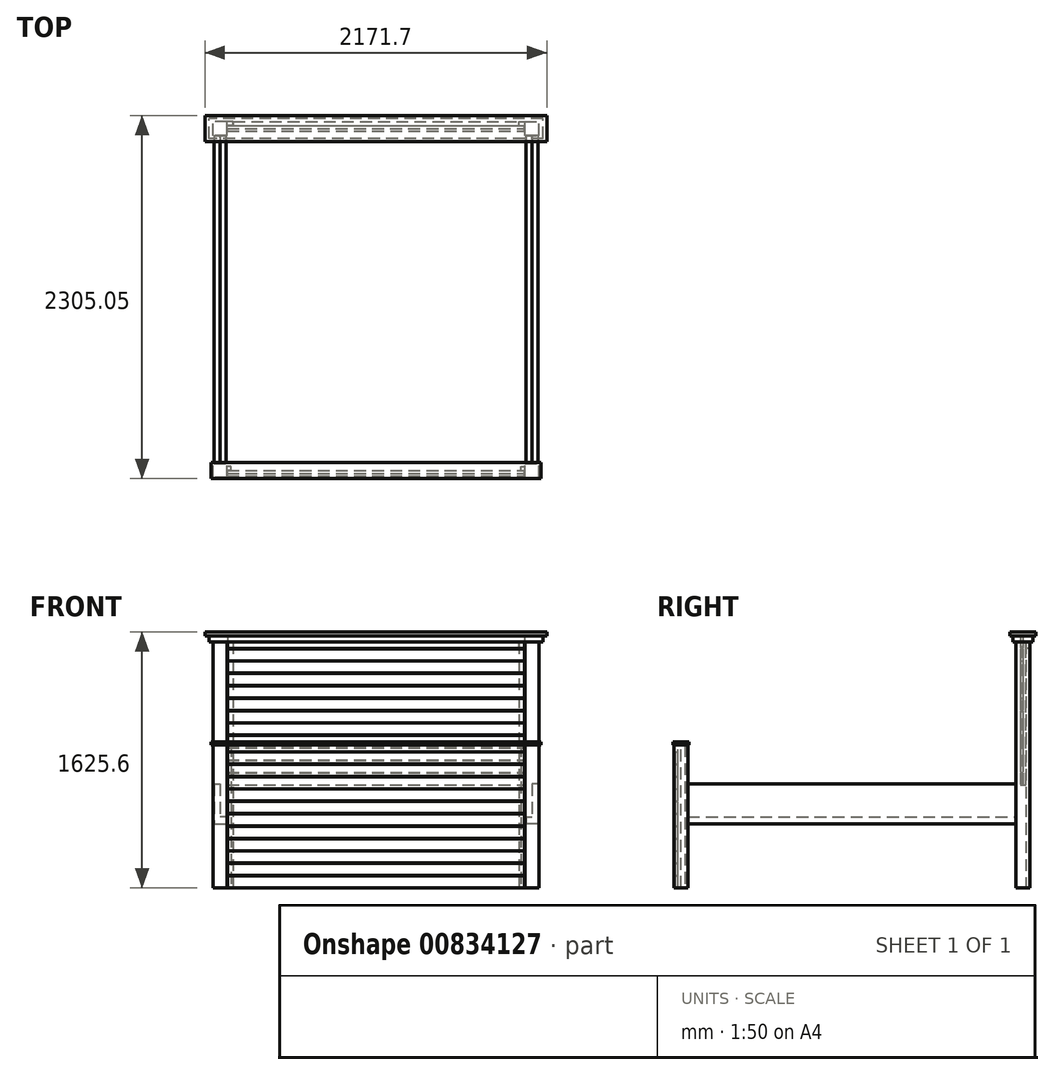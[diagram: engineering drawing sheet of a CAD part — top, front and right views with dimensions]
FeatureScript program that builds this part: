
annotation { "Feature Type Name" : "Feature", "Feature Type Description" : "" }
export const myFeature = defineFeature(function(context is Context, id is Id, definition is map)
    precondition{}
    {
        {
            var Q0;
            Q0=qCreatedBy(makeId("Top.planeOp"),FACE);
            var sketch = newSketch(context, id + "F0", { "sketchPlane" : qUnion([Q0])});
            skLineSegment(sketch, "E0.rect.bottom", {"start": v(44.45, -44.45) * mm, "end": v(-44.45, -44.45) * mm});
            skLineSegment(sketch, "E0.rect.top", {"start": v(44.45, 44.45) * mm, "end": v(-44.45, 44.45) * mm});
            skLineSegment(sketch, "E0.rect.left", {"start": v(44.45, -44.45) * mm, "end": v(44.45, 44.45) * mm});
            skLineSegment(sketch, "E0.rect.right", {"start": v(-44.45, -44.45) * mm, "end": v(-44.45, 44.45) * mm});
            skPoint(sketch, "E0.rect.middle", {"position": v(0, 0) * mm});
            skSolve(sketch);
        }
        {
            var Q0;
            Q0=qSketchRegion(id+"F0",true);
            extrude(context, id + "F1", {"entities" : qUnion([Q0]), "depth" : 906.78 * mm});
        }
        {
            var Q0;
            Q0=makeQuery(id+"F1.opExtrude","SWEPT_FACE",FACE,{"disambiguationData":[OSD([sQuery(id+"F0.wireOp",EDGE,"E0.rect.left")])]});
            var sketch = newSketch(context, id + "F2", { "sketchPlane" : qUnion([Q0])});
            skLineSegment(sketch, "E1.bottom", {"start": v(0, 906.78) * mm, "end": v(25.4, 906.78) * mm});
            skLineSegment(sketch, "E1.top", {"start": v(0, 0) * mm, "end": v(25.4, 0) * mm});
            skLineSegment(sketch, "E1.left", {"start": v(0, 906.78) * mm, "end": v(0, 0) * mm});
            skLineSegment(sketch, "E1.right", {"start": v(25.4, 906.78) * mm, "end": v(25.4, 0) * mm});
            skSolve(sketch);
        }
        {
            var Q0;
            Q0=qSketchRegion(id+"F2",true);
            extrude(context, id + "F3", {"entities" : qUnion([Q0]), "depth" : 25.4 * mm});
        }
        {
            var Q0;
            Q0=qCreatedBy(makeId("Right.planeOp"),FACE);
            cPlane(context, id + "F4", {"entities" : qUnion([Q0]), "cplaneType" : CPlaneType.OFFSET, "offset" : 990.6 * mm, "width" : 152.4 * mm, "height" : 152.4 * mm});
        }
        {
            var Q0;
            Q0=makeQuery(id+"F1.opExtrude","SWEPT_BODY",BODY,{"disambiguationData":[OSD([sQuery(id+"F0.wireOp",EDGE,"E0.rect.bottom"),sQuery(id+"F0.wireOp",EDGE,"E0.rect.top"),sQuery(id+"F0.wireOp",EDGE,"E0.rect.left"),sQuery(id+"F0.wireOp",EDGE,"E0.rect.right")])]});
            var Q1;
            Q1=makeQuery(id+"F3.opExtrude","SWEPT_BODY",BODY,{"disambiguationData":[OSD([sQuery(id+"F2.wireOp",EDGE,"E1.bottom"),sQuery(id+"F2.wireOp",EDGE,"E1.top"),sQuery(id+"F2.wireOp",EDGE,"E1.left"),sQuery(id+"F2.wireOp",EDGE,"E1.right")])]});
            var Q2;
            Q2=qCreatedBy(id+"F4.planeOp",FACE);
            mirror(context, id + "F5", {"entities" : qUnion([Q0, Q1]), "mirrorPlane" : qUnion([Q2])});
        }
        {
            var Q0;
            Q0=makeQuery(id+"F1.opExtrude","CAP_FACE",FACE,{"disambiguationData":[OSD([sQuery(id+"F0.wireOp",EDGE,"E0.rect.bottom"),sQuery(id+"F0.wireOp",EDGE,"E0.rect.top"),sQuery(id+"F0.wireOp",EDGE,"E0.rect.left"),sQuery(id+"F0.wireOp",EDGE,"E0.rect.right")])],"isStart":false});
            var sketch = newSketch(context, id + "F6", { "sketchPlane" : qUnion([Q0])});
            skLineSegment(sketch, "E2", {"start": v(0, 0) * mm, "end": v(1981.2, 0) * mm, "construction": true});
            skPoint(sketch, "E2.endSnap0", {"position": v(44.45, 0) * mm});
            skLineSegment(sketch, "E3", {"start": v(1936.75, 44.45) * mm, "end": v(2025.65, -44.45) * mm, "construction": true});
            skLineSegment(sketch, "E4.rect.bottom", {"start": v(-57.15, -50.8) * mm, "end": v(2038.35, -50.8) * mm});
            skLineSegment(sketch, "E4.rect.top", {"start": v(-57.15, 50.8) * mm, "end": v(2038.35, 50.8) * mm});
            skLineSegment(sketch, "E4.rect.left", {"start": v(-57.15, -50.8) * mm, "end": v(-57.15, 50.8) * mm});
            skLineSegment(sketch, "E4.rect.right", {"start": v(2038.35, -50.8) * mm, "end": v(2038.35, 50.8) * mm});
            skPoint(sketch, "E4.rect.middle", {"position": v(990.6, 0) * mm});
            skSolve(sketch);
        }
        {
            var Q0;
            Q0=qSketchRegion(id+"F6",true);
            extrude(context, id + "F7", {"entities" : qUnion([Q0]), "depth" : 19.05 * mm});
        }
        {
            var Q0;
            Q0=makeQuery(id+"F3.opExtrude","SWEPT_FACE",FACE,{"disambiguationData":[OSD([sQuery(id+"F2.wireOp",EDGE,"E1.left")])]});
            var sketch = newSketch(context, id + "F8", { "sketchPlane" : qUnion([Q0])});
            skLineSegment(sketch, "E5", {"start": v(44.45, 906.78) * mm, "end": v(1936.75, 0) * mm, "construction": true});
            skLineSegment(sketch, "E6.rect.bottom", {"start": v(46.99, 0) * mm, "end": v(1934.2, 0) * mm});
            skLineSegment(sketch, "E6.rect.top", {"start": v(46.99, 906.78) * mm, "end": v(1934.21, 906.78) * mm});
            skLineSegment(sketch, "E6.rect.left", {"start": v(47, 0) * mm, "end": v(47, 906.78) * mm});
            skLineSegment(sketch, "E6.rect.right", {"start": v(1934.2, 0) * mm, "end": v(1934.2, 906.78) * mm});
            skPoint(sketch, "E6.rect.middle", {"position": v(990.6, 453.4) * mm});
            skSolve(sketch);
        }
        {
            var Q0;
            Q0=qSketchRegion(id+"F8",true);
            extrude(context, id + "F9", {"entities" : qUnion([Q0]), "depth" : 19.05 * mm});
        }
        {
            var Q0;
            Q0=makeQuery(id+"F9.opExtrude","CAP_FACE",FACE,{"disambiguationData":[OSD([sQuery(id+"F8.wireOp",EDGE,"E6.rect.bottom"),sQuery(id+"F8.wireOp",EDGE,"E6.rect.top"),sQuery(id+"F8.wireOp",EDGE,"E6.rect.left"),sQuery(id+"F8.wireOp",EDGE,"E6.rect.right")])],"isStart":false});
            var sketch = newSketch(context, id + "F10", { "sketchPlane" : qUnion([Q0])});
            skLineSegment(sketch, "E7.bottom", {"start": v(46.99, 76.2) * mm, "end": v(1934.2, 76.2) * mm});
            skLineSegment(sketch, "E7.top", {"start": v(46.99, 0) * mm, "end": v(1934.2, 0) * mm});
            skLineSegment(sketch, "E7.left", {"start": v(47, 76.2) * mm, "end": v(47, 0) * mm});
            skLineSegment(sketch, "E7.right", {"start": v(1934.2, 76.2) * mm, "end": v(1934.2, 0) * mm});
            skLineSegment(sketch, "E8.0.1.0", {"start": v(47, 154.94) * mm, "end": v(47, 78.74) * mm});
            skLineSegment(sketch, "E8.0.1.1", {"start": v(46.99, 154.94) * mm, "end": v(1934.2, 154.94) * mm});
            skLineSegment(sketch, "E8.0.1.2", {"start": v(46.99, 78.74) * mm, "end": v(1934.2, 78.74) * mm});
            skLineSegment(sketch, "E8.0.1.3", {"start": v(1934.2, 154.94) * mm, "end": v(1934.2, 78.74) * mm});
            skLineSegment(sketch, "E8.0.2.0", {"start": v(47, 233.68) * mm, "end": v(47, 157.48) * mm});
            skLineSegment(sketch, "E8.0.2.1", {"start": v(46.99, 233.68) * mm, "end": v(1934.2, 233.68) * mm});
            skLineSegment(sketch, "E8.0.2.2", {"start": v(46.99, 157.48) * mm, "end": v(1934.2, 157.48) * mm});
            skLineSegment(sketch, "E8.0.2.3", {"start": v(1934.2, 233.68) * mm, "end": v(1934.2, 157.48) * mm});
            skLineSegment(sketch, "E8.0.3.0", {"start": v(47, 312.42) * mm, "end": v(47, 236.22) * mm});
            skLineSegment(sketch, "E8.0.3.1", {"start": v(46.99, 312.42) * mm, "end": v(1934.2, 312.42) * mm});
            skLineSegment(sketch, "E8.0.3.2", {"start": v(46.99, 236.22) * mm, "end": v(1934.2, 236.22) * mm});
            skLineSegment(sketch, "E8.0.3.3", {"start": v(1934.2, 312.42) * mm, "end": v(1934.2, 236.22) * mm});
            skLineSegment(sketch, "E8.0.4.0", {"start": v(47, 391.16) * mm, "end": v(47, 314.96) * mm});
            skLineSegment(sketch, "E8.0.4.1", {"start": v(46.99, 391.16) * mm, "end": v(1934.2, 391.16) * mm});
            skLineSegment(sketch, "E8.0.4.2", {"start": v(46.99, 314.96) * mm, "end": v(1934.2, 314.96) * mm});
            skLineSegment(sketch, "E8.0.4.3", {"start": v(1934.2, 391.16) * mm, "end": v(1934.2, 314.96) * mm});
            skLineSegment(sketch, "E8.0.5.0", {"start": v(47, 469.9) * mm, "end": v(47, 393.7) * mm});
            skLineSegment(sketch, "E8.0.5.1", {"start": v(46.99, 469.9) * mm, "end": v(1934.2, 469.9) * mm});
            skLineSegment(sketch, "E8.0.5.2", {"start": v(46.99, 393.7) * mm, "end": v(1934.2, 393.7) * mm});
            skLineSegment(sketch, "E8.0.5.3", {"start": v(1934.2, 469.9) * mm, "end": v(1934.2, 393.7) * mm});
            skLineSegment(sketch, "E8.direction1", {"start": v(47, 0) * mm, "end": v(72.4, 0) * mm, "construction": true});
            skLineSegment(sketch, "E8.direction2", {"start": v(47, 0) * mm, "end": v(47, 78.74) * mm, "construction": true});
            skLineSegment(sketch, "E9.0.0.6", {"start": v(47, 548.64) * mm, "end": v(47, 472.44) * mm});
            skLineSegment(sketch, "E9.3.0.6", {"start": v(46.99, 548.64) * mm, "end": v(1934.2, 548.64) * mm});
            skLineSegment(sketch, "E9.6.0.6", {"start": v(46.99, 472.44) * mm, "end": v(1934.2, 472.44) * mm});
            skLineSegment(sketch, "E9.9.0.6", {"start": v(1934.2, 548.64) * mm, "end": v(1934.2, 472.44) * mm});
            skLineSegment(sketch, "E10.0.0.7", {"start": v(47, 627.38) * mm, "end": v(47, 551.18) * mm});
            skLineSegment(sketch, "E10.3.0.7", {"start": v(46.99, 627.38) * mm, "end": v(1934.2, 627.38) * mm});
            skLineSegment(sketch, "E10.6.0.7", {"start": v(46.99, 551.18) * mm, "end": v(1934.2, 551.18) * mm});
            skLineSegment(sketch, "E10.9.0.7", {"start": v(1934.2, 627.38) * mm, "end": v(1934.2, 551.18) * mm});
            skLineSegment(sketch, "E10.0.0.8", {"start": v(47, 706.12) * mm, "end": v(47, 629.92) * mm});
            skLineSegment(sketch, "E10.3.0.8", {"start": v(46.99, 706.12) * mm, "end": v(1934.2, 706.12) * mm});
            skLineSegment(sketch, "E10.6.0.8", {"start": v(46.99, 629.92) * mm, "end": v(1934.2, 629.92) * mm});
            skLineSegment(sketch, "E10.9.0.8", {"start": v(1934.2, 706.12) * mm, "end": v(1934.2, 629.92) * mm});
            skLineSegment(sketch, "E10.0.0.9", {"start": v(47, 784.86) * mm, "end": v(47, 708.66) * mm});
            skLineSegment(sketch, "E10.3.0.9", {"start": v(46.99, 784.86) * mm, "end": v(1934.2, 784.86) * mm});
            skLineSegment(sketch, "E10.6.0.9", {"start": v(46.99, 708.66) * mm, "end": v(1934.2, 708.66) * mm});
            skLineSegment(sketch, "E10.9.0.9", {"start": v(1934.2, 784.86) * mm, "end": v(1934.2, 708.66) * mm});
            skLineSegment(sketch, "E11.0.0.10", {"start": v(47, 863.6) * mm, "end": v(47, 787.4) * mm});
            skLineSegment(sketch, "E11.3.0.10", {"start": v(46.99, 863.6) * mm, "end": v(1934.2, 863.6) * mm});
            skLineSegment(sketch, "E11.6.0.10", {"start": v(46.99, 787.4) * mm, "end": v(1934.2, 787.4) * mm});
            skLineSegment(sketch, "E11.9.0.10", {"start": v(1934.2, 863.6) * mm, "end": v(1934.2, 787.4) * mm});
            skSolve(sketch);
        }
        {
            var Q0;
            Q0=qSketchRegion(id+"F10",true);
            extrude(context, id + "F11", {"entities" : qUnion([Q0]), "depth" : 15.88 * mm});
        }
        {
            var Q0;
            Q0=makeQuery(id+"F1.opExtrude","SWEPT_FACE",FACE,{"disambiguationData":[OSD([sQuery(id+"F0.wireOp",EDGE,"E0.rect.top")])]});
            var sketch = newSketch(context, id + "F12", { "sketchPlane" : qUnion([Q0])});
            skLineSegment(sketch, "E12.bottom", {"start": v(38.1, 660.4) * mm, "end": v(0, 660.4) * mm});
            skLineSegment(sketch, "E12.top", {"start": v(38.1, 406.4) * mm, "end": v(0, 406.4) * mm});
            skLineSegment(sketch, "E12.left", {"start": v(38.1, 660.4) * mm, "end": v(38.1, 406.4) * mm});
            skLineSegment(sketch, "E12.right", {"start": v(0, 660.4) * mm, "end": v(0, 406.4) * mm});
            skSolve(sketch);
        }
        {
            var Q0;
            Q0=qSketchRegion(id+"F12",true);
            extrude(context, id + "F13", {"entities" : qUnion([Q0]), "depth" : 2082.8 * mm});
        }
        {
            var Q0;
            Q0=makeQuery(id+"F13.opExtrude","SWEPT_FACE",FACE,{"disambiguationData":[OSD([sQuery(id+"F12.wireOp",EDGE,"E12.right")])]});
            var sketch = newSketch(context, id + "F14", { "sketchPlane" : qUnion([Q0])});
            skLineSegment(sketch, "E13.bottom", {"start": v(44.45, 450.85) * mm, "end": v(2127.25, 450.85) * mm});
            skLineSegment(sketch, "E13.top", {"start": v(44.45, 406.4) * mm, "end": v(2127.25, 406.4) * mm});
            skLineSegment(sketch, "E13.left", {"start": v(44.45, 450.85) * mm, "end": v(44.45, 406.4) * mm});
            skLineSegment(sketch, "E13.right", {"start": v(2127.25, 450.85) * mm, "end": v(2127.25, 406.4) * mm});
            skSolve(sketch);
        }
        {
            var Q0;
            Q0=qSketchRegion(id+"F14",true);
            extrude(context, id + "F15", {"entities" : qUnion([Q0]), "depth" : 38.1 * mm});
        }
        {
            var Q0;
            Q0=makeQuery(id+"F13.opExtrude","SWEPT_BODY",BODY,{"disambiguationData":[OSD([sQuery(id+"F12.wireOp",EDGE,"E12.bottom"),sQuery(id+"F12.wireOp",EDGE,"E12.top"),sQuery(id+"F12.wireOp",EDGE,"E12.left"),sQuery(id+"F12.wireOp",EDGE,"E12.right")])]});
            var Q1;
            Q1=makeQuery(id+"F15.opExtrude","SWEPT_BODY",BODY,{"disambiguationData":[OSD([sQuery(id+"F14.wireOp",EDGE,"E13.bottom"),sQuery(id+"F14.wireOp",EDGE,"E13.top"),sQuery(id+"F14.wireOp",EDGE,"E13.left"),sQuery(id+"F14.wireOp",EDGE,"E13.right")])]});
            var Q2;
            Q2=qCreatedBy(id+"F4.planeOp",FACE);
            mirror(context, id + "F16", {"operationType" : NewBodyOperationType.ADD, "entities" : qUnion([Q0, Q1]), "mirrorPlane" : qUnion([Q2])});
        }
        {
            var Q0;
            Q0=qCreatedBy(makeId("Top.planeOp"),FACE);
            var sketch = newSketch(context, id + "F17", { "sketchPlane" : qUnion([Q0])});
            skLineSegment(sketch, "E14.rect.bottom", {"start": v(44.45, 2127.25) * mm, "end": v(-44.45, 2127.25) * mm});
            skLineSegment(sketch, "E14.rect.top", {"start": v(44.45, 2216.15) * mm, "end": v(-44.45, 2216.15) * mm});
            skLineSegment(sketch, "E14.rect.left", {"start": v(44.45, 2127.25) * mm, "end": v(44.45, 2216.15) * mm});
            skLineSegment(sketch, "E14.rect.right", {"start": v(-44.45, 2127.25) * mm, "end": v(-44.45, 2216.15) * mm});
            skPoint(sketch, "E14.rect.middle", {"position": v(0, 2171.7) * mm});
            skLineSegment(sketch, "E15.rect.bottom", {"start": v(1936.75, 2127.25) * mm, "end": v(2025.65, 2127.25) * mm});
            skLineSegment(sketch, "E15.rect.top", {"start": v(1936.75, 2216.15) * mm, "end": v(2025.65, 2216.15) * mm});
            skLineSegment(sketch, "E15.rect.left", {"start": v(1936.75, 2127.25) * mm, "end": v(1936.75, 2216.15) * mm});
            skLineSegment(sketch, "E15.rect.right", {"start": v(2025.65, 2127.25) * mm, "end": v(2025.65, 2216.15) * mm});
            skPoint(sketch, "E15.rect.middle", {"position": v(1981.2, 2171.7) * mm});
            skSolve(sketch);
        }
        {
            var Q0;
            Q0=qSketchRegion(id+"F17",true);
            extrude(context, id + "F18", {"entities" : qUnion([Q0]), "depth" : 1562.1 * mm});
        }
        {
            var Q0;
            Q0=makeQuery(id+"F18.opExtrude","SWEPT_FACE",FACE,{"disambiguationData":[OSD([sQuery(id+"F17.wireOp",EDGE,"E14.rect.left")])]});
            var sketch = newSketch(context, id + "F19", { "sketchPlane" : qUnion([Q0])});
            skLineSegment(sketch, "E16.bottom", {"start": v(2216.15, 1562.1) * mm, "end": v(2190.75, 1562.1) * mm});
            skLineSegment(sketch, "E16.top", {"start": v(2216.15, 0) * mm, "end": v(2171.7, 0) * mm});
            skLineSegment(sketch, "E16.left", {"start": v(2216.15, 1562.1) * mm, "end": v(2216.15, 0) * mm});
            skLineSegment(sketch, "E16.right", {"start": v(2190.75, 1562.1) * mm, "end": v(2190.75, 0) * mm});
            skSolve(sketch);
        }
        {
            var Q0;
            Q0=qSketchRegion(id+"F19",true);
            extrude(context, id + "F20", {"entities" : qUnion([Q0]), "depth" : 38.1 * mm});
        }
        {
            var Q0;
            Q0=makeQuery(id+"F20.opExtrude","SWEPT_BODY",BODY,{"disambiguationData":[OSD([sQuery(id+"F19.wireOp",EDGE,"E16.bottom"),sQuery(id+"F19.wireOp",EDGE,"E16.top"),sQuery(id+"F19.wireOp",EDGE,"E16.left"),sQuery(id+"F19.wireOp",EDGE,"E16.right")])]});
            var Q1;
            Q1=qCreatedBy(id+"F4.planeOp",FACE);
            mirror(context, id + "F21", {"entities" : qUnion([Q0]), "mirrorPlane" : qUnion([Q1])});
        }
        {
            var Q0;
            Q0=makeQuery(id+"F18.opExtrude","CAP_FACE",FACE,{"disambiguationData":[OSD([sQuery(id+"F17.wireOp",EDGE,"E14.rect.bottom"),sQuery(id+"F17.wireOp",EDGE,"E14.rect.top"),sQuery(id+"F17.wireOp",EDGE,"E14.rect.left"),sQuery(id+"F17.wireOp",EDGE,"E14.rect.right")])],"isStart":false});
            var sketch = newSketch(context, id + "F22", { "sketchPlane" : qUnion([Q0])});
            skLineSegment(sketch, "E17", {"start": v(44.45, 2171.7) * mm, "end": v(1936.75, 2171.7) * mm, "construction": true});
            skPoint(sketch, "E17.endSnap0", {"position": v(44.45, 2171.7) * mm});
            skLineSegment(sketch, "E18.rect.bottom", {"start": v(2051.05, 2108.2) * mm, "end": v(-69.85, 2108.2) * mm});
            skLineSegment(sketch, "E18.rect.top", {"start": v(2051.05, 2235.2) * mm, "end": v(-69.85, 2235.2) * mm});
            skLineSegment(sketch, "E18.rect.left", {"start": v(2051.05, 2108.2) * mm, "end": v(2051.05, 2235.2) * mm});
            skLineSegment(sketch, "E18.rect.right", {"start": v(-69.85, 2108.2) * mm, "end": v(-69.85, 2235.2) * mm});
            skPoint(sketch, "E18.rect.middle", {"position": v(990.6, 2171.7) * mm});
            skSolve(sketch);
        }
        {
            var Q0;
            Q0=qSketchRegion(id+"F22",true);
            extrude(context, id + "F23", {"entities" : qUnion([Q0]), "depth" : 38.1 * mm});
        }
        {
            var Q0;
            Q0=makeQuery(id+"F23.opExtrude","CAP_FACE",FACE,{"disambiguationData":[OSD([sQuery(id+"F22.wireOp",EDGE,"E18.rect.bottom"),sQuery(id+"F22.wireOp",EDGE,"E18.rect.top"),sQuery(id+"F22.wireOp",EDGE,"E18.rect.left"),sQuery(id+"F22.wireOp",EDGE,"E18.rect.right")])],"isStart":true});
            var sketch = newSketch(context, id + "F24", { "sketchPlane" : qUnion([Q0])});
            skLineSegment(sketch, "E19.bottom", {"start": v(85.1, -2190.75) * mm, "end": v(1898.65, -2190.75) * mm});
            skLineSegment(sketch, "E19.top", {"start": v(85.1, -2216.15) * mm, "end": v(1898.65, -2216.15) * mm});
            skLineSegment(sketch, "E19.left", {"start": v(85.1, -2190.75) * mm, "end": v(85.1, -2216.15) * mm});
            skLineSegment(sketch, "E19.right", {"start": v(1898.65, -2190.75) * mm, "end": v(1898.65, -2216.15) * mm});
            skSolve(sketch);
        }
        {
            var Q0;
            Q0=qSketchRegion(id+"F24",true);
            extrude(context, id + "F25", {"entities" : qUnion([Q0]), "depth" : 38.1 * mm});
        }
        {
            var Q0;
            Q0=makeQuery(id+"F20.opExtrude","SWEPT_FACE",FACE,{"disambiguationData":[OSD([sQuery(id+"F19.wireOp",EDGE,"E16.right")])]});
            var sketch = newSketch(context, id + "F26", { "sketchPlane" : qUnion([Q0])});
            skLineSegment(sketch, "E20", {"start": v(44.45, 1562.1) * mm, "end": v(1936.75, 654.05) * mm, "construction": true});
            skLineSegment(sketch, "E21.rect.bottom", {"start": v(46.04, 655.64) * mm, "end": v(1935.16, 655.64) * mm});
            skLineSegment(sketch, "E21.rect.top", {"start": v(46.04, 1560.51) * mm, "end": v(1935.16, 1560.51) * mm});
            skLineSegment(sketch, "E21.rect.left", {"start": v(46.04, 655.64) * mm, "end": v(46.04, 1560.51) * mm});
            skLineSegment(sketch, "E21.rect.right", {"start": v(1935.16, 655.64) * mm, "end": v(1935.16, 1560.51) * mm});
            skPoint(sketch, "E21.rect.middle", {"position": v(990.6, 1108.07) * mm});
            skSolve(sketch);
        }
        {
            var Q0;
            Q0=qSketchRegion(id+"F26",true);
            extrude(context, id + "F27", {"entities" : qUnion([Q0]), "depth" : 19.05 * mm});
        }
        {
            var Q0;
            Q0=makeQuery(id+"F27.opExtrude","CAP_FACE",FACE,{"disambiguationData":[OSD([sQuery(id+"F26.wireOp",EDGE,"E21.rect.bottom"),sQuery(id+"F26.wireOp",EDGE,"E21.rect.top"),sQuery(id+"F26.wireOp",EDGE,"E21.rect.left"),sQuery(id+"F26.wireOp",EDGE,"E21.rect.right")])],"isStart":false});
            var sketch = newSketch(context, id + "F28", { "sketchPlane" : qUnion([Q0])});
            skLineSegment(sketch, "E22.bottom", {"start": v(47, 731.84) * mm, "end": v(1934.21, 731.84) * mm});
            skLineSegment(sketch, "E22.top", {"start": v(46.99, 655.64) * mm, "end": v(1934.21, 655.64) * mm});
            skLineSegment(sketch, "E22.left", {"start": v(46.99, 731.84) * mm, "end": v(46.99, 655.64) * mm});
            skLineSegment(sketch, "E22.right", {"start": v(1934.21, 731.84) * mm, "end": v(1934.21, 655.64) * mm});
            skLineSegment(sketch, "E23.0.1.0", {"start": v(46.99, 810.58) * mm, "end": v(1934.21, 810.58) * mm});
            skLineSegment(sketch, "E23.0.1.1", {"start": v(1934.21, 810.58) * mm, "end": v(1934.21, 734.38) * mm});
            skLineSegment(sketch, "E23.0.1.2", {"start": v(47, 734.38) * mm, "end": v(1934.21, 734.38) * mm});
            skLineSegment(sketch, "E23.0.1.3", {"start": v(46.99, 810.58) * mm, "end": v(46.99, 734.38) * mm});
            skLineSegment(sketch, "E23.0.2.0", {"start": v(46.99, 889.32) * mm, "end": v(1934.21, 889.32) * mm});
            skLineSegment(sketch, "E23.0.2.1", {"start": v(1934.21, 889.32) * mm, "end": v(1934.21, 813.12) * mm});
            skLineSegment(sketch, "E23.0.2.2", {"start": v(47, 813.12) * mm, "end": v(1934.21, 813.12) * mm});
            skLineSegment(sketch, "E23.0.2.3", {"start": v(46.99, 889.32) * mm, "end": v(46.99, 813.12) * mm});
            skLineSegment(sketch, "E23.0.3.0", {"start": v(46.99, 968.06) * mm, "end": v(1934.21, 968.06) * mm});
            skLineSegment(sketch, "E23.0.3.1", {"start": v(1934.21, 968.06) * mm, "end": v(1934.21, 891.86) * mm});
            skLineSegment(sketch, "E23.0.3.2", {"start": v(47, 891.86) * mm, "end": v(1934.21, 891.86) * mm});
            skLineSegment(sketch, "E23.0.3.3", {"start": v(46.99, 968.06) * mm, "end": v(46.99, 891.86) * mm});
            skLineSegment(sketch, "E23.0.4.0", {"start": v(46.99, 1046.8) * mm, "end": v(1934.21, 1046.8) * mm});
            skLineSegment(sketch, "E23.0.4.1", {"start": v(1934.21, 1046.8) * mm, "end": v(1934.21, 970.6) * mm});
            skLineSegment(sketch, "E23.0.4.2", {"start": v(47, 970.6) * mm, "end": v(1934.21, 970.6) * mm});
            skLineSegment(sketch, "E23.0.4.3", {"start": v(46.99, 1046.8) * mm, "end": v(46.99, 970.6) * mm});
            skLineSegment(sketch, "E23.0.5.0", {"start": v(46.99, 1125.54) * mm, "end": v(1934.21, 1125.54) * mm});
            skLineSegment(sketch, "E23.0.5.1", {"start": v(1934.21, 1125.54) * mm, "end": v(1934.21, 1049.34) * mm});
            skLineSegment(sketch, "E23.0.5.2", {"start": v(47, 1049.34) * mm, "end": v(1934.21, 1049.34) * mm});
            skLineSegment(sketch, "E23.0.5.3", {"start": v(46.99, 1125.54) * mm, "end": v(46.99, 1049.34) * mm});
            skLineSegment(sketch, "E23.direction1", {"start": v(47, 731.84) * mm, "end": v(72.39, 731.84) * mm, "construction": true});
            skLineSegment(sketch, "E23.direction2", {"start": v(46.99, 731.84) * mm, "end": v(46.99, 810.58) * mm, "construction": true});
            skLineSegment(sketch, "E24.0.0.6", {"start": v(46.99, 1204.28) * mm, "end": v(1934.21, 1204.28) * mm});
            skLineSegment(sketch, "E24.3.0.6", {"start": v(1934.21, 1204.28) * mm, "end": v(1934.21, 1128.08) * mm});
            skLineSegment(sketch, "E24.6.0.6", {"start": v(47, 1128.08) * mm, "end": v(1934.21, 1128.08) * mm});
            skLineSegment(sketch, "E24.9.0.6", {"start": v(46.99, 1204.28) * mm, "end": v(46.99, 1128.08) * mm});
            skLineSegment(sketch, "E25.0.0.7", {"start": v(46.99, 1283.02) * mm, "end": v(1934.21, 1283.02) * mm});
            skLineSegment(sketch, "E25.3.0.7", {"start": v(1934.21, 1283.02) * mm, "end": v(1934.21, 1206.82) * mm});
            skLineSegment(sketch, "E25.6.0.7", {"start": v(47, 1206.82) * mm, "end": v(1934.21, 1206.82) * mm});
            skLineSegment(sketch, "E25.9.0.7", {"start": v(46.99, 1283.02) * mm, "end": v(46.99, 1206.82) * mm});
            skLineSegment(sketch, "E25.0.0.8", {"start": v(46.99, 1361.76) * mm, "end": v(1934.21, 1361.76) * mm});
            skLineSegment(sketch, "E25.3.0.8", {"start": v(1934.21, 1361.76) * mm, "end": v(1934.21, 1285.56) * mm});
            skLineSegment(sketch, "E25.6.0.8", {"start": v(46.99, 1285.56) * mm, "end": v(1934.2, 1285.56) * mm});
            skLineSegment(sketch, "E25.9.0.8", {"start": v(46.99, 1361.76) * mm, "end": v(46.99, 1285.56) * mm});
            skLineSegment(sketch, "E25.0.0.9", {"start": v(46.99, 1440.5) * mm, "end": v(1934.21, 1440.5) * mm});
            skLineSegment(sketch, "E25.3.0.9", {"start": v(1934.21, 1440.5) * mm, "end": v(1934.21, 1364.3) * mm});
            skLineSegment(sketch, "E25.6.0.9", {"start": v(46.99, 1364.3) * mm, "end": v(1934.2, 1364.3) * mm});
            skLineSegment(sketch, "E25.9.0.9", {"start": v(46.99, 1440.5) * mm, "end": v(46.99, 1364.3) * mm});
            skLineSegment(sketch, "E25.0.0.10", {"start": v(46.99, 1519.24) * mm, "end": v(1934.21, 1519.24) * mm});
            skLineSegment(sketch, "E25.3.0.10", {"start": v(1934.21, 1519.24) * mm, "end": v(1934.21, 1443.04) * mm});
            skLineSegment(sketch, "E25.6.0.10", {"start": v(46.99, 1443.04) * mm, "end": v(1934.2, 1443.04) * mm});
            skLineSegment(sketch, "E25.9.0.10", {"start": v(46.99, 1519.24) * mm, "end": v(46.99, 1443.04) * mm});
            skLineSegment(sketch, "E25.0.0.11", {"start": v(46.99, 1597.98) * mm, "end": v(1934.21, 1597.98) * mm});
            skLineSegment(sketch, "E25.3.0.11", {"start": v(1934.21, 1597.98) * mm, "end": v(1934.21, 1521.78) * mm});
            skLineSegment(sketch, "E25.6.0.11", {"start": v(46.99, 1521.78) * mm, "end": v(1934.2, 1521.78) * mm});
            skLineSegment(sketch, "E25.9.0.11", {"start": v(46.99, 1597.98) * mm, "end": v(46.99, 1521.78) * mm});
            skSolve(sketch);
        }
        {
            var Q0;
            Q0=qSketchRegion(id+"F28",true);
            extrude(context, id + "F29", {"entities" : qUnion([Q0]), "depth" : 15.88 * mm});
        }
        {
            var Q0;
            Q0=makeQuery(id+"F23.opExtrude","CAP_FACE",FACE,{"disambiguationData":[OSD([sQuery(id+"F22.wireOp",EDGE,"E18.rect.bottom"),sQuery(id+"F22.wireOp",EDGE,"E18.rect.top"),sQuery(id+"F22.wireOp",EDGE,"E18.rect.left"),sQuery(id+"F22.wireOp",EDGE,"E18.rect.right")])],"isStart":false});
            var sketch = newSketch(context, id + "F30", { "sketchPlane" : qUnion([Q0])});
            skLineSegment(sketch, "E26", {"start": v(990.6, 2235.2) * mm, "end": v(990.6, 2108.2) * mm, "construction": true});
            skLineSegment(sketch, "E27.rect.bottom", {"start": v(-95.25, 2089.15) * mm, "end": v(2076.45, 2089.15) * mm});
            skLineSegment(sketch, "E27.rect.top", {"start": v(-95.25, 2254.25) * mm, "end": v(2076.45, 2254.25) * mm});
            skLineSegment(sketch, "E27.rect.left", {"start": v(-95.25, 2089.15) * mm, "end": v(-95.25, 2254.25) * mm});
            skLineSegment(sketch, "E27.rect.right", {"start": v(2076.45, 2089.15) * mm, "end": v(2076.45, 2254.25) * mm});
            skPoint(sketch, "E27.rect.middle", {"position": v(990.6, 2171.7) * mm});
            skSolve(sketch);
        }
        {
            var Q0;
            Q0=qSketchRegion(id+"F30",true);
            var Q1;
            Q1=qConstructionFilter(qBodyType(qCreatedBy(id+"F30",EDGE),BodyType.WIRE),ConstructionObject.NO);
            extrude(context, id + "F31", {"entities" : qUnion([Q0]), "surfaceEntities" : qUnion([Q1]), "depth" : 25.4 * mm});
        }
    });
